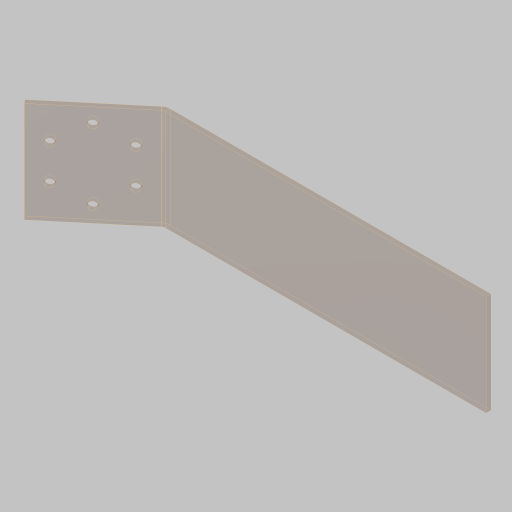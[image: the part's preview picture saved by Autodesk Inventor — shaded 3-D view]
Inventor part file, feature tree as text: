
AUTODESK INVENTOR PART (.ipt)
format: ipt  version: 2023.5 (Build 275446000, 446)  size: 127,488 bytes
history: native  units: in
note: dims shown in document units (in); Inventor stores cm internally (conversion verified against a paired STEP export)
features: sheet_metal_op x4, sketch x3, other x2, hole x1
ambient origin geometry x8: Origin, YZ Plane, XZ Plane, XY Plane, X Axis, Y Axis, Z Axis, Center Point
bodies: Solid1 (feature_tree)
feature tree (10):
  sheet_metal_op  "Face1"
  sheet_metal_op  "Flange1"
  hole  "Hole1"  [1 undecoded]
  sketch  "Sketch1"  dims[d0=2.5in d1=8.0in]
  other  "Plate1"
  sketch  "Sketch2"  dims[d2=0.12in]
  other  "Plate2"
  sheet_metal_op  "Bend1"
  sheet_metal_op  "Corner1"
  sketch  "Sketch3"  dims[d3=0.12in d4=0.06in d5=0.24in d6=0.12in d7=2.5in d8=0.2749in d9=0.12in d10=0.48in d11=0.12in d12=0.12in d13=1.75in d14=2.3622in d16=360.0deg d18=0.201in d19=0.75in d20=0.385in d21=0.063in d22=0.5635in d23=0.12in d24=0.8108in]
note: 1 required parameter value undecoded (feature->parameter linkage not recoverable at this tier; creation-order binding heuristic only, values carry confidence <= 0.55)
